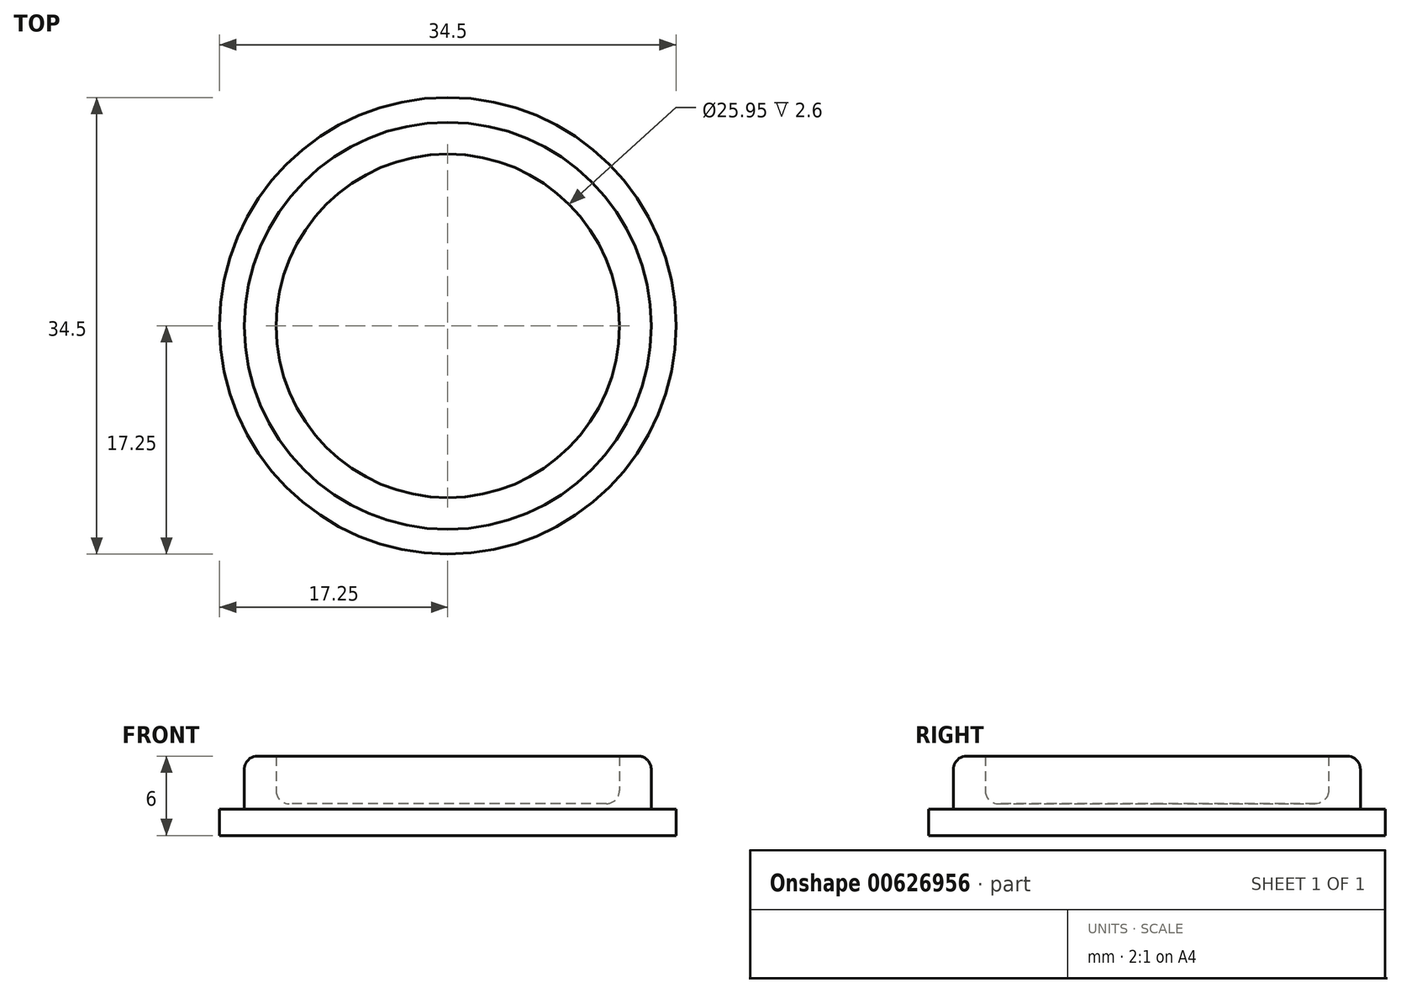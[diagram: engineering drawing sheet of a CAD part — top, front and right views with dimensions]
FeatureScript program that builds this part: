
annotation { "Feature Type Name" : "Feature", "Feature Type Description" : "" }
export const myFeature = defineFeature(function(context is Context, id is Id, definition is map)
    precondition{}
    {
        {
            var Q0;
            Q0=qCreatedBy(makeId("Top.planeOp"),FACE);
            var sketch = newSketch(context, id + "F0", { "sketchPlane" : qUnion([Q0])});
            skCircle(sketch, "E0", {"center": v(0, 0) * mm, "radius": 15.37 * mm});
            skCircle(sketch, "E1", {"center": v(0, 0) * mm, "radius": 17.25 * mm});
            skSolve(sketch);
        }
        {
            var Q0;
            Q0=makeQuery(id+"F0.imprint","IMPRINT",FACE,{"disambiguationData":[TD([[makeQuery(id+"F0.imprint","IMPRINT",EDGE,{"derivedFrom":sQuery(id+"F0.wireOp",EDGE,"E0")}),1.0]])]});
            extrude(context, id + "F1", {"entities" : qUnion([Q0]), "depth" : 6 * mm, "offsetDistance" : 25 * mm});
        }
        {
            var Q0;
            Q0=makeQuery(id+"F0.imprint","IMPRINT",FACE,{"disambiguationData":[TD([[makeQuery(id+"F0.imprint","IMPRINT",EDGE,{"derivedFrom":sQuery(id+"F0.wireOp",EDGE,"E0")}),-1.0]])]});
            extrude(context, id + "F2", {"entities" : qUnion([Q0]), "operationType" : NewBodyOperationType.ADD, "depth" : 2 * mm, "offsetDistance" : 25 * mm});
        }
        {
            var Q0;
            Q0=makeQuery(id+"F1.opExtrude","CAP_FACE",FACE,{"disambiguationData":[OSD([sQuery(id+"F0.wireOp",EDGE,"E0")])],"isStart":false});
            shell(context, id + "F3", {"entities" : qUnion([Q0]), "thickness" : 2.4 * mm});
        }
        {
            var Q0;
            Q0=makeQuery(id+"F1.opExtrude","CAP_EDGE",EDGE,{"disambiguationData":[OSD([sQuery(id+"F0.wireOp",EDGE,"E0")])],"isStart":false});
            var Q1;
            {var subQ0=sQuery(id+"F0.wireOp",EDGE,"E0");Q1=makeQuery(id+"F3.opShell","TWEAK_EDGE",EDGE,{"derivedFrom":[makeQuery(id+"F2.boolean.opBoolean","MERGE",FACE,{"derivedFrom":[makeQuery(id+"F1.opExtrude","CAP_FACE",FACE,{"disambiguationData":[OSD([subQ0])],"isStart":true}),makeQuery(id+"F2.opExtrude","CAP_FACE",FACE,{"disambiguationData":[OSD([subQ0,sQuery(id+"F0.wireOp",EDGE,"E1")])],"isStart":true})]}),makeQuery(id+"F1.opExtrude","SWEPT_FACE",FACE,{"disambiguationData":[OSD([subQ0])]})]});}
            fillet(context, id + "F4", {"entities" : qUnion([Q0, Q1]), "radius" : 1 * mm, "tangentPropagation" : true, "allowEdgeOverflow" : false});
        }
    });
